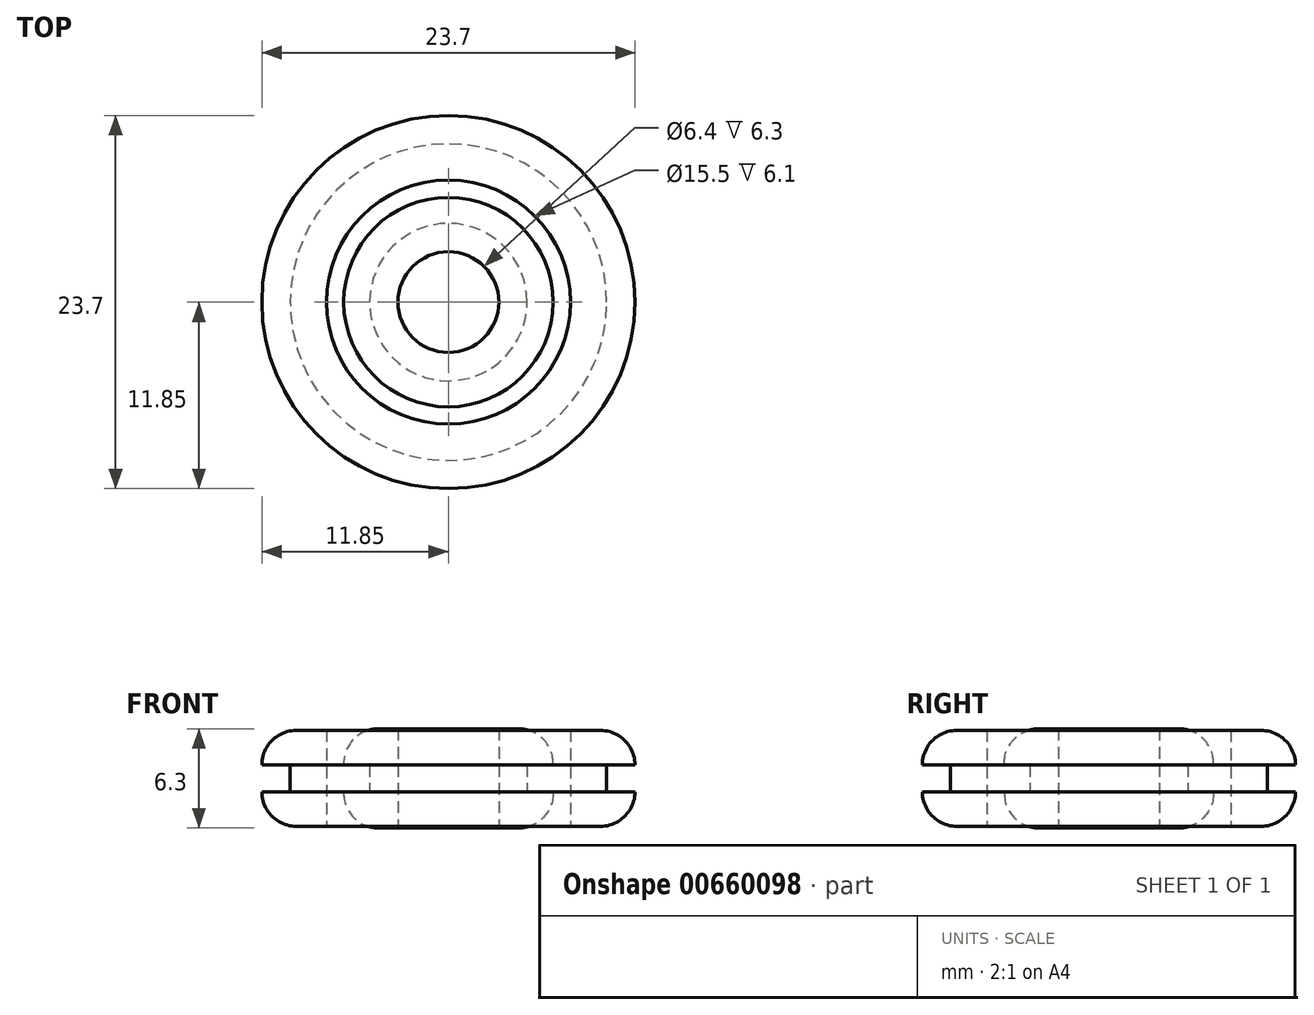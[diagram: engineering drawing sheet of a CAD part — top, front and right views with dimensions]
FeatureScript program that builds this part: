
annotation { "Feature Type Name" : "Feature", "Feature Type Description" : "" }
export const myFeature = defineFeature(function(context is Context, id is Id, definition is map)
    precondition{}
    {
        {
            var Q0;
            Q0=qCreatedBy(makeId("Front.planeOp"),FACE);
            var sketch = newSketch(context, id + "F0", { "sketchPlane" : qUnion([Q0])});
            skLineSegment(sketch, "E0", {"start": v(0, 0) * mm, "end": v(0, 3.05) * mm, "construction": true});
            skLineSegment(sketch, "E1", {"start": v(-7.75, 3.05) * mm, "end": v(-7.75, -3.05) * mm});
            skLineSegment(sketch, "E2", {"start": v(-7.75, -3.05) * mm, "end": v(-9.65, -3.05) * mm});
            skLineSegment(sketch, "E3", {"start": v(-11.85, -0.85) * mm, "end": v(-11.85, -0.85) * mm});
            skLineSegment(sketch, "E4", {"start": v(-11.85, -0.85) * mm, "end": v(-10.05, -0.85) * mm});
            skLineSegment(sketch, "E5", {"start": v(-10.05, -0.85) * mm, "end": v(-10.05, 0.85) * mm});
            skLineSegment(sketch, "E6", {"start": v(-10.05, 0.85) * mm, "end": v(-11.85, 0.85) * mm});
            skLineSegment(sketch, "E7", {"start": v(-11.85, 0.85) * mm, "end": v(-11.85, 0.85) * mm});
            skLineSegment(sketch, "E8", {"start": v(-9.65, 3.05) * mm, "end": v(-7.75, 3.05) * mm});
            skPoint(sketch, "E9", {"position": v(-7.75, 0) * mm});
            skPoint(sketch, "E10", {"position": v(-10.05, 0) * mm});
            skPoint(sketch, "E11.visualSharp", {"position": v(-11.85, 3.05) * mm});
            skArc(sketch, "E11.filletArc", {"start": v(-9.65, 3.05) * mm, "mid": v(-11.2, 2.4) * mm, "end": v(-11.85, 0.85) * mm});
            skPoint(sketch, "E12.visualSharp", {"position": v(-11.85, -3.05) * mm});
            skArc(sketch, "E12.filletArc", {"start": v(-11.85, -0.85) * mm, "mid": v(-11.2, -2.4) * mm, "end": v(-9.65, -3.05) * mm});
            skSolve(sketch);
        }
        {
            var Q0;
            Q0=makeQuery(id+"F0.imprint","IMPRINT",FACE,{"disambiguationData":[TD([[makeQuery(id+"F0.imprint","IMPRINT",EDGE,{"derivedFrom":sQuery(id+"F0.wireOp",EDGE,"E1")}),-1.0]])]});
            var Q1;
            Q1=sQuery(id+"F0.wireOp",EDGE,"E0");
            revolve(context, id + "F1", {"entities" : qUnion([Q0]), "axis" : qUnion([Q1]), "revolveType" : RevolveType.FULL});
        }
        {
            var Q0;
            Q0=qCreatedBy(makeId("Front.planeOp"),FACE);
            var sketch = newSketch(context, id + "F2", { "sketchPlane" : qUnion([Q0])});
            skLineSegment(sketch, "E13", {"start": v(0, 0) * mm, "end": v(0, 3.15) * mm, "construction": true});
            skLineSegment(sketch, "E14", {"start": v(-3.2, 3.15) * mm, "end": v(-3.2, -3.15) * mm});
            skLineSegment(sketch, "E15", {"start": v(-3.2, -3.15) * mm, "end": v(-4.45, -3.15) * mm});
            skLineSegment(sketch, "E16", {"start": v(-6.65, -0.95) * mm, "end": v(-6.65, -0.85) * mm});
            skLineSegment(sketch, "E17", {"start": v(-6.65, -0.85) * mm, "end": v(-5, -0.85) * mm});
            skLineSegment(sketch, "E18", {"start": v(-5, -0.85) * mm, "end": v(-5, 0.85) * mm});
            skLineSegment(sketch, "E19", {"start": v(-5, 0.85) * mm, "end": v(-6.65, 0.85) * mm});
            skLineSegment(sketch, "E20", {"start": v(-6.65, 0.85) * mm, "end": v(-6.65, 0.95) * mm});
            skLineSegment(sketch, "E21", {"start": v(-4.45, 3.15) * mm, "end": v(-3.2, 3.15) * mm});
            skPoint(sketch, "E22", {"position": v(-3.2, 0) * mm});
            skPoint(sketch, "E23", {"position": v(-5, 0) * mm});
            skPoint(sketch, "E24.visualSharp", {"position": v(-6.65, 3.15) * mm});
            skArc(sketch, "E24.filletArc", {"start": v(-4.45, 3.15) * mm, "mid": v(-6, 2.5) * mm, "end": v(-6.65, 0.95) * mm});
            skPoint(sketch, "E25.visualSharp", {"position": v(-6.65, -3.15) * mm});
            skArc(sketch, "E25.filletArc", {"start": v(-6.65, -0.95) * mm, "mid": v(-6, -2.5) * mm, "end": v(-4.45, -3.15) * mm});
            skSolve(sketch);
        }
        {
            var Q0;
            Q0=makeQuery(id+"F2.imprint","IMPRINT",FACE,{"disambiguationData":[TD([[makeQuery(id+"F2.imprint","IMPRINT",EDGE,{"derivedFrom":sQuery(id+"F2.wireOp",EDGE,"E14")}),-1.0]])]});
            var Q1;
            Q1=sQuery(id+"F2.wireOp",EDGE,"E13");
            revolve(context, id + "F3", {"entities" : qUnion([Q0]), "axis" : qUnion([Q1]), "revolveType" : RevolveType.FULL});
        }
    });
